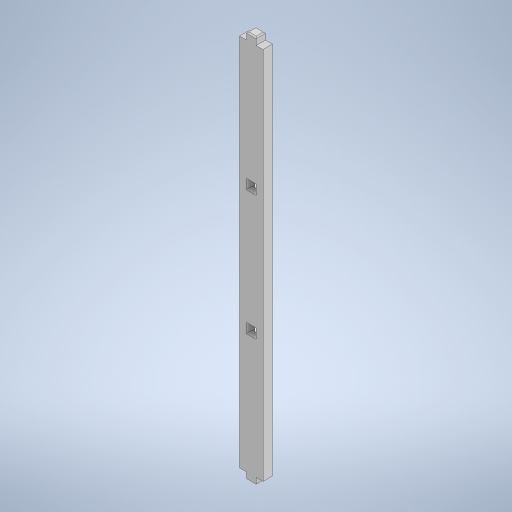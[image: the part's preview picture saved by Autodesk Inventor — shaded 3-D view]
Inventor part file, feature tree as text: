
AUTODESK INVENTOR PART (.ipt)
format: ipt  version: 2024 (Build 280153000, 153)  size: 299,008 bytes
history: native  units: in
note: dims shown in document units (in); Inventor stores cm internally (conversion verified against a paired STEP export)
features: chamfer x2, extrude x1, sketch x1
ambient origin geometry x8: Origin, YZ Plane, XZ Plane, XY Plane, X Axis, Y Axis, Z Axis, Center Point
bodies: Solid1 (feature_tree)
feature tree (4):
  extrude  "Extrusion1"  Depth=6.5256in
  chamfer  "Chamfer1"  Distance=0.1575in
  chamfer  "Chamfer2"  Distance=0.1614in
  sketch  "Sketch1"  dims[d0=0.3937in d1=6.5256in d2=0.1575in d3=0.0in d4=0.1614in d5=0.1614in d6=1.935in d7=0.1614in d8=0.1614in d9=0.1969in d10=0.1181in d11=0.1181in d12=0.0197in d13=0.0787in d14=45.0deg d15=0.0591in d16=0.0787in d17=45.0deg]
